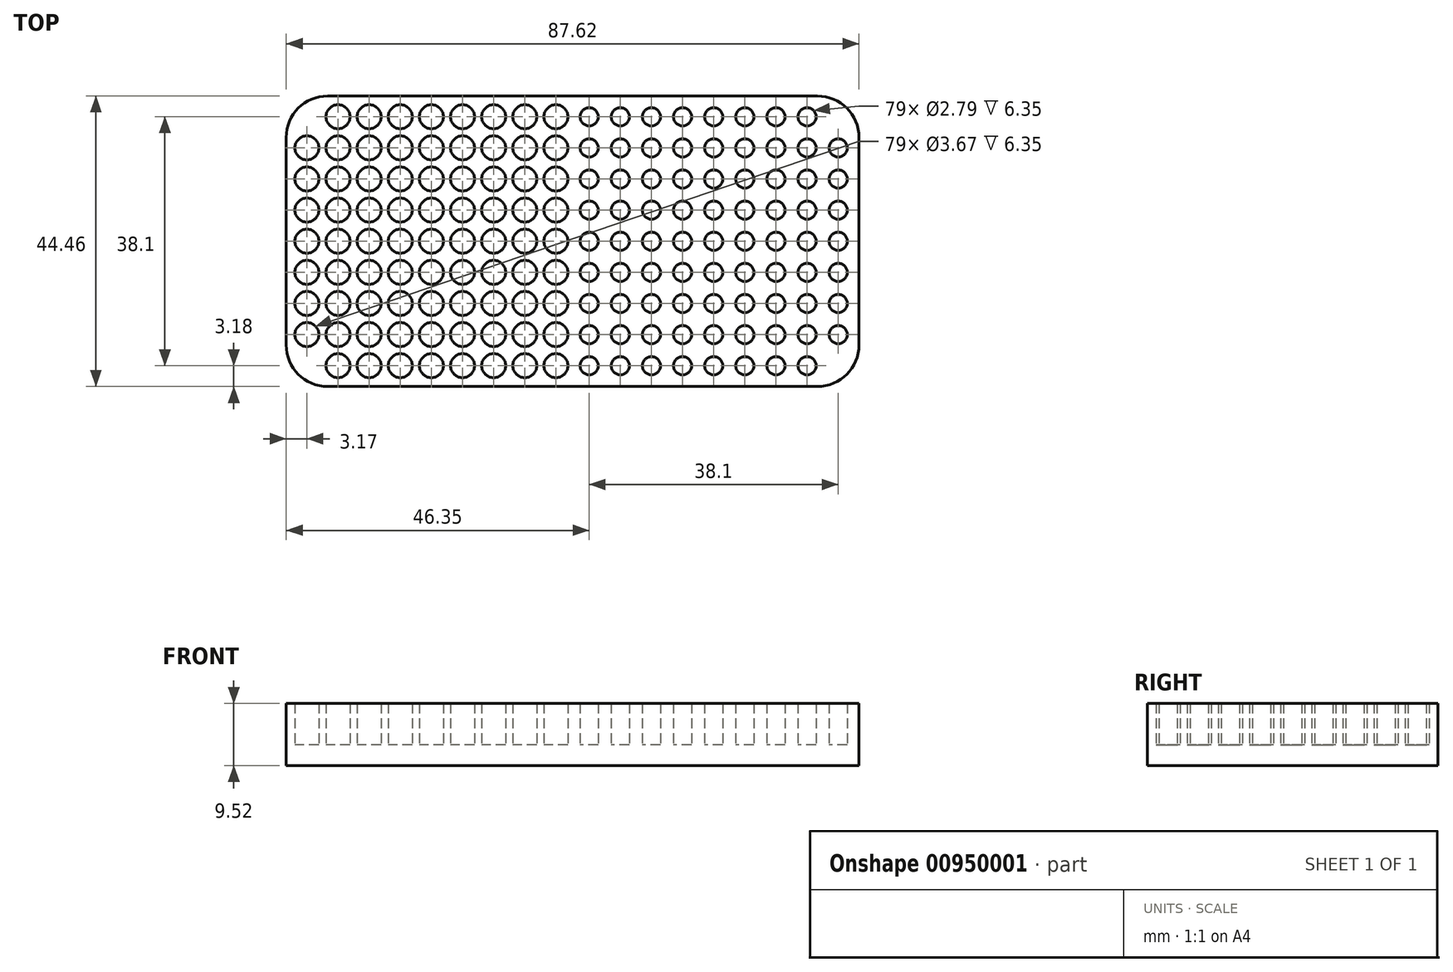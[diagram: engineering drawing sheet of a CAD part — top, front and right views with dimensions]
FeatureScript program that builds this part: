
annotation { "Feature Type Name" : "Feature", "Feature Type Description" : "" }
export const myFeature = defineFeature(function(context is Context, id is Id, definition is map)
    precondition{}
    {
        {
            var Q0;
            Q0=qCreatedBy(makeId("Top.planeOp"),FACE);
            var sketch = newSketch(context, id + "F0", { "sketchPlane" : qUnion([Q0])});
            skLineSegment(sketch, "E0.bottom", {"start": v(43.82, 22.23) * mm, "end": v(-43.82, 22.23) * mm});
            skLineSegment(sketch, "E0.top", {"start": v(43.82, -22.23) * mm, "end": v(-43.82, -22.23) * mm});
            skLineSegment(sketch, "E0.left", {"start": v(43.82, 22.23) * mm, "end": v(43.82, -22.23) * mm});
            skLineSegment(sketch, "E0.right", {"start": v(-43.82, 22.23) * mm, "end": v(-43.82, -22.23) * mm});
            skPoint(sketch, "E0.middle", {"position": v(0, 0) * mm});
            skCircle(sketch, "E1", {"center": v(-40.64, 19.05) * mm, "radius": 1.84 * mm, "construction": true});
            skCircle(sketch, "E2", {"center": v(40.64, 19.05) * mm, "radius": 1.4 * mm, "construction": true});
            skCircle(sketch, "E3.0.1.0", {"center": v(-40.64, 14.29) * mm, "radius": 1.84 * mm});
            skCircle(sketch, "E3.0.2.0", {"center": v(-40.64, 9.53) * mm, "radius": 1.84 * mm});
            skCircle(sketch, "E3.0.3.0", {"center": v(-40.64, 4.76) * mm, "radius": 1.84 * mm});
            skCircle(sketch, "E3.0.4.0", {"center": v(-40.64, 0) * mm, "radius": 1.84 * mm});
            skCircle(sketch, "E3.0.5.0", {"center": v(-40.64, -4.76) * mm, "radius": 1.84 * mm});
            skCircle(sketch, "E3.0.6.0", {"center": v(-40.64, -9.52) * mm, "radius": 1.84 * mm});
            skCircle(sketch, "E3.0.7.0", {"center": v(-40.64, -14.29) * mm, "radius": 1.84 * mm});
            skCircle(sketch, "E3.1.0.0", {"center": v(-35.88, 19.05) * mm, "radius": 1.84 * mm});
            skCircle(sketch, "E3.1.1.0", {"center": v(-35.88, 14.29) * mm, "radius": 1.84 * mm});
            skCircle(sketch, "E3.1.2.0", {"center": v(-35.88, 9.53) * mm, "radius": 1.84 * mm});
            skCircle(sketch, "E3.1.3.0", {"center": v(-35.88, 4.76) * mm, "radius": 1.84 * mm});
            skCircle(sketch, "E3.1.4.0", {"center": v(-35.88, 0) * mm, "radius": 1.84 * mm});
            skCircle(sketch, "E3.1.5.0", {"center": v(-35.88, -4.76) * mm, "radius": 1.84 * mm});
            skCircle(sketch, "E3.1.6.0", {"center": v(-35.88, -9.52) * mm, "radius": 1.84 * mm});
            skCircle(sketch, "E3.1.7.0", {"center": v(-35.88, -14.29) * mm, "radius": 1.84 * mm});
            skCircle(sketch, "E3.2.0.0", {"center": v(-31.12, 19.05) * mm, "radius": 1.84 * mm});
            skCircle(sketch, "E3.2.1.0", {"center": v(-31.12, 14.29) * mm, "radius": 1.84 * mm});
            skCircle(sketch, "E3.2.2.0", {"center": v(-31.12, 9.53) * mm, "radius": 1.84 * mm});
            skCircle(sketch, "E3.2.3.0", {"center": v(-31.12, 4.76) * mm, "radius": 1.84 * mm});
            skCircle(sketch, "E3.2.4.0", {"center": v(-31.12, 0) * mm, "radius": 1.84 * mm});
            skCircle(sketch, "E3.2.5.0", {"center": v(-31.12, -4.76) * mm, "radius": 1.84 * mm});
            skCircle(sketch, "E3.2.6.0", {"center": v(-31.12, -9.52) * mm, "radius": 1.84 * mm});
            skCircle(sketch, "E3.2.7.0", {"center": v(-31.12, -14.29) * mm, "radius": 1.84 * mm});
            skCircle(sketch, "E3.3.0.0", {"center": v(-26.35, 19.05) * mm, "radius": 1.84 * mm});
            skCircle(sketch, "E3.3.1.0", {"center": v(-26.35, 14.29) * mm, "radius": 1.84 * mm});
            skCircle(sketch, "E3.3.2.0", {"center": v(-26.35, 9.53) * mm, "radius": 1.84 * mm});
            skCircle(sketch, "E3.3.3.0", {"center": v(-26.35, 4.76) * mm, "radius": 1.84 * mm});
            skCircle(sketch, "E3.3.4.0", {"center": v(-26.35, 0) * mm, "radius": 1.84 * mm});
            skCircle(sketch, "E3.3.5.0", {"center": v(-26.35, -4.76) * mm, "radius": 1.84 * mm});
            skCircle(sketch, "E3.3.6.0", {"center": v(-26.35, -9.52) * mm, "radius": 1.84 * mm});
            skCircle(sketch, "E3.3.7.0", {"center": v(-26.35, -14.29) * mm, "radius": 1.84 * mm});
            skCircle(sketch, "E3.4.0.0", {"center": v(-21.59, 19.05) * mm, "radius": 1.84 * mm});
            skCircle(sketch, "E3.4.1.0", {"center": v(-21.59, 14.29) * mm, "radius": 1.84 * mm});
            skCircle(sketch, "E3.4.2.0", {"center": v(-21.59, 9.53) * mm, "radius": 1.84 * mm});
            skCircle(sketch, "E3.4.3.0", {"center": v(-21.59, 4.76) * mm, "radius": 1.84 * mm});
            skCircle(sketch, "E3.4.4.0", {"center": v(-21.59, 0) * mm, "radius": 1.84 * mm});
            skCircle(sketch, "E3.4.5.0", {"center": v(-21.59, -4.76) * mm, "radius": 1.84 * mm});
            skCircle(sketch, "E3.4.6.0", {"center": v(-21.59, -9.52) * mm, "radius": 1.84 * mm});
            skCircle(sketch, "E3.4.7.0", {"center": v(-21.59, -14.29) * mm, "radius": 1.84 * mm});
            skCircle(sketch, "E3.5.0.0", {"center": v(-16.83, 19.05) * mm, "radius": 1.84 * mm});
            skCircle(sketch, "E3.5.1.0", {"center": v(-16.83, 14.29) * mm, "radius": 1.84 * mm});
            skCircle(sketch, "E3.5.2.0", {"center": v(-16.83, 9.53) * mm, "radius": 1.84 * mm});
            skCircle(sketch, "E3.5.3.0", {"center": v(-16.83, 4.76) * mm, "radius": 1.84 * mm});
            skCircle(sketch, "E3.5.4.0", {"center": v(-16.83, 0) * mm, "radius": 1.84 * mm});
            skCircle(sketch, "E3.5.5.0", {"center": v(-16.83, -4.76) * mm, "radius": 1.84 * mm});
            skCircle(sketch, "E3.5.6.0", {"center": v(-16.83, -9.52) * mm, "radius": 1.84 * mm});
            skCircle(sketch, "E3.5.7.0", {"center": v(-16.83, -14.29) * mm, "radius": 1.84 * mm});
            skCircle(sketch, "E3.6.0.0", {"center": v(-12.06, 19.05) * mm, "radius": 1.84 * mm});
            skCircle(sketch, "E3.6.1.0", {"center": v(-12.06, 14.29) * mm, "radius": 1.84 * mm});
            skCircle(sketch, "E3.6.2.0", {"center": v(-12.06, 9.53) * mm, "radius": 1.84 * mm});
            skCircle(sketch, "E3.6.3.0", {"center": v(-12.06, 4.76) * mm, "radius": 1.84 * mm});
            skCircle(sketch, "E3.6.4.0", {"center": v(-12.06, 0) * mm, "radius": 1.84 * mm});
            skCircle(sketch, "E3.6.5.0", {"center": v(-12.06, -4.76) * mm, "radius": 1.84 * mm});
            skCircle(sketch, "E3.6.6.0", {"center": v(-12.06, -9.52) * mm, "radius": 1.84 * mm});
            skCircle(sketch, "E3.6.7.0", {"center": v(-12.06, -14.29) * mm, "radius": 1.84 * mm});
            skCircle(sketch, "E3.7.0.0", {"center": v(-7.3, 19.05) * mm, "radius": 1.84 * mm});
            skCircle(sketch, "E3.7.1.0", {"center": v(-7.3, 14.29) * mm, "radius": 1.84 * mm});
            skCircle(sketch, "E3.7.2.0", {"center": v(-7.3, 9.53) * mm, "radius": 1.84 * mm});
            skCircle(sketch, "E3.7.3.0", {"center": v(-7.3, 4.76) * mm, "radius": 1.84 * mm});
            skCircle(sketch, "E3.7.4.0", {"center": v(-7.3, 0) * mm, "radius": 1.84 * mm});
            skCircle(sketch, "E3.7.5.0", {"center": v(-7.3, -4.76) * mm, "radius": 1.84 * mm});
            skCircle(sketch, "E3.7.6.0", {"center": v(-7.3, -9.52) * mm, "radius": 1.84 * mm});
            skCircle(sketch, "E3.7.7.0", {"center": v(-7.3, -14.29) * mm, "radius": 1.84 * mm});
            skCircle(sketch, "E3.8.0.0", {"center": v(-2.54, 19.05) * mm, "radius": 1.84 * mm});
            skCircle(sketch, "E3.8.1.0", {"center": v(-2.54, 14.29) * mm, "radius": 1.84 * mm});
            skCircle(sketch, "E3.8.2.0", {"center": v(-2.54, 9.53) * mm, "radius": 1.84 * mm});
            skCircle(sketch, "E3.8.3.0", {"center": v(-2.54, 4.76) * mm, "radius": 1.84 * mm});
            skCircle(sketch, "E3.8.4.0", {"center": v(-2.54, 0) * mm, "radius": 1.84 * mm});
            skCircle(sketch, "E3.8.5.0", {"center": v(-2.54, -4.76) * mm, "radius": 1.84 * mm});
            skCircle(sketch, "E3.8.6.0", {"center": v(-2.54, -9.52) * mm, "radius": 1.84 * mm});
            skCircle(sketch, "E3.8.7.0", {"center": v(-2.54, -14.29) * mm, "radius": 1.84 * mm});
            skLineSegment(sketch, "E3.direction1", {"start": v(-40.64, 19.05) * mm, "end": v(-35.88, 19.05) * mm, "construction": true});
            skLineSegment(sketch, "E3.direction2", {"start": v(-40.64, 19.05) * mm, "end": v(-40.64, 14.29) * mm, "construction": true});
            skCircle(sketch, "E4.0.0.8", {"center": v(-40.64, -19.05) * mm, "radius": 1.84 * mm, "construction": true});
            skCircle(sketch, "E4.0.1.8", {"center": v(-35.88, -19.05) * mm, "radius": 1.84 * mm});
            skCircle(sketch, "E4.0.2.8", {"center": v(-31.11, -19.05) * mm, "radius": 1.84 * mm});
            skCircle(sketch, "E4.0.3.8", {"center": v(-26.35, -19.05) * mm, "radius": 1.84 * mm});
            skCircle(sketch, "E4.0.4.8", {"center": v(-21.59, -19.05) * mm, "radius": 1.84 * mm});
            skCircle(sketch, "E4.0.5.8", {"center": v(-16.83, -19.05) * mm, "radius": 1.84 * mm});
            skCircle(sketch, "E4.0.6.8", {"center": v(-12.06, -19.05) * mm, "radius": 1.84 * mm});
            skCircle(sketch, "E4.0.7.8", {"center": v(-7.3, -19.05) * mm, "radius": 1.84 * mm});
            skCircle(sketch, "E4.0.8.8", {"center": v(-2.54, -19.05) * mm, "radius": 1.84 * mm});
            skCircle(sketch, "E5.0.1.0", {"center": v(40.64, 14.29) * mm, "radius": 1.4 * mm});
            skCircle(sketch, "E5.0.2.0", {"center": v(40.64, 9.53) * mm, "radius": 1.4 * mm});
            skCircle(sketch, "E5.0.3.0", {"center": v(40.64, 4.76) * mm, "radius": 1.4 * mm});
            skCircle(sketch, "E5.0.4.0", {"center": v(40.64, 0) * mm, "radius": 1.4 * mm});
            skCircle(sketch, "E5.0.5.0", {"center": v(40.64, -4.76) * mm, "radius": 1.4 * mm});
            skCircle(sketch, "E5.0.6.0", {"center": v(40.64, -9.52) * mm, "radius": 1.4 * mm});
            skCircle(sketch, "E5.0.7.0", {"center": v(40.64, -14.29) * mm, "radius": 1.4 * mm});
            skCircle(sketch, "E5.0.8.0", {"center": v(40.64, -19.05) * mm, "radius": 1.4 * mm, "construction": true});
            skCircle(sketch, "E5.1.0.0", {"center": v(35.88, 19.05) * mm, "radius": 1.4 * mm});
            skCircle(sketch, "E5.1.1.0", {"center": v(35.88, 14.29) * mm, "radius": 1.4 * mm});
            skCircle(sketch, "E5.1.2.0", {"center": v(35.88, 9.53) * mm, "radius": 1.4 * mm});
            skCircle(sketch, "E5.1.3.0", {"center": v(35.88, 4.76) * mm, "radius": 1.4 * mm});
            skCircle(sketch, "E5.1.4.0", {"center": v(35.88, 0) * mm, "radius": 1.4 * mm});
            skCircle(sketch, "E5.1.5.0", {"center": v(35.88, -4.76) * mm, "radius": 1.4 * mm});
            skCircle(sketch, "E5.1.6.0", {"center": v(35.88, -9.52) * mm, "radius": 1.4 * mm});
            skCircle(sketch, "E5.1.7.0", {"center": v(35.88, -14.29) * mm, "radius": 1.4 * mm});
            skCircle(sketch, "E5.1.8.0", {"center": v(35.88, -19.05) * mm, "radius": 1.4 * mm});
            skCircle(sketch, "E5.2.0.0", {"center": v(31.12, 19.05) * mm, "radius": 1.4 * mm});
            skCircle(sketch, "E5.2.1.0", {"center": v(31.12, 14.29) * mm, "radius": 1.4 * mm});
            skCircle(sketch, "E5.2.2.0", {"center": v(31.12, 9.53) * mm, "radius": 1.4 * mm});
            skCircle(sketch, "E5.2.3.0", {"center": v(31.12, 4.76) * mm, "radius": 1.4 * mm});
            skCircle(sketch, "E5.2.4.0", {"center": v(31.12, 0) * mm, "radius": 1.4 * mm});
            skCircle(sketch, "E5.2.5.0", {"center": v(31.12, -4.76) * mm, "radius": 1.4 * mm});
            skCircle(sketch, "E5.2.6.0", {"center": v(31.12, -9.52) * mm, "radius": 1.4 * mm});
            skCircle(sketch, "E5.2.7.0", {"center": v(31.12, -14.29) * mm, "radius": 1.4 * mm});
            skCircle(sketch, "E5.2.8.0", {"center": v(31.12, -19.05) * mm, "radius": 1.4 * mm});
            skCircle(sketch, "E5.3.0.0", {"center": v(26.35, 19.05) * mm, "radius": 1.4 * mm});
            skCircle(sketch, "E5.3.1.0", {"center": v(26.35, 14.29) * mm, "radius": 1.4 * mm});
            skCircle(sketch, "E5.3.2.0", {"center": v(26.35, 9.53) * mm, "radius": 1.4 * mm});
            skCircle(sketch, "E5.3.3.0", {"center": v(26.35, 4.76) * mm, "radius": 1.4 * mm});
            skCircle(sketch, "E5.3.4.0", {"center": v(26.35, 0) * mm, "radius": 1.4 * mm});
            skCircle(sketch, "E5.3.5.0", {"center": v(26.35, -4.76) * mm, "radius": 1.4 * mm});
            skCircle(sketch, "E5.3.6.0", {"center": v(26.35, -9.52) * mm, "radius": 1.4 * mm});
            skCircle(sketch, "E5.3.7.0", {"center": v(26.35, -14.29) * mm, "radius": 1.4 * mm});
            skCircle(sketch, "E5.3.8.0", {"center": v(26.35, -19.05) * mm, "radius": 1.4 * mm});
            skCircle(sketch, "E5.4.0.0", {"center": v(21.6, 19.05) * mm, "radius": 1.4 * mm});
            skCircle(sketch, "E5.4.1.0", {"center": v(21.6, 14.29) * mm, "radius": 1.4 * mm});
            skCircle(sketch, "E5.4.2.0", {"center": v(21.6, 9.53) * mm, "radius": 1.4 * mm});
            skCircle(sketch, "E5.4.3.0", {"center": v(21.6, 4.76) * mm, "radius": 1.4 * mm});
            skCircle(sketch, "E5.4.4.0", {"center": v(21.6, 0) * mm, "radius": 1.4 * mm});
            skCircle(sketch, "E5.4.5.0", {"center": v(21.6, -4.76) * mm, "radius": 1.4 * mm});
            skCircle(sketch, "E5.4.6.0", {"center": v(21.6, -9.52) * mm, "radius": 1.4 * mm});
            skCircle(sketch, "E5.4.7.0", {"center": v(21.6, -14.29) * mm, "radius": 1.4 * mm});
            skCircle(sketch, "E5.4.8.0", {"center": v(21.6, -19.05) * mm, "radius": 1.4 * mm});
            skCircle(sketch, "E5.5.0.0", {"center": v(16.83, 19.05) * mm, "radius": 1.4 * mm});
            skCircle(sketch, "E5.5.1.0", {"center": v(16.83, 14.29) * mm, "radius": 1.4 * mm});
            skCircle(sketch, "E5.5.2.0", {"center": v(16.83, 9.53) * mm, "radius": 1.4 * mm});
            skCircle(sketch, "E5.5.3.0", {"center": v(16.83, 4.76) * mm, "radius": 1.4 * mm});
            skCircle(sketch, "E5.5.4.0", {"center": v(16.83, 0) * mm, "radius": 1.4 * mm});
            skCircle(sketch, "E5.5.5.0", {"center": v(16.83, -4.76) * mm, "radius": 1.4 * mm});
            skCircle(sketch, "E5.5.6.0", {"center": v(16.83, -9.52) * mm, "radius": 1.4 * mm});
            skCircle(sketch, "E5.5.7.0", {"center": v(16.83, -14.29) * mm, "radius": 1.4 * mm});
            skCircle(sketch, "E5.5.8.0", {"center": v(16.83, -19.05) * mm, "radius": 1.4 * mm});
            skCircle(sketch, "E5.6.0.0", {"center": v(12.07, 19.05) * mm, "radius": 1.4 * mm});
            skCircle(sketch, "E5.6.1.0", {"center": v(12.07, 14.29) * mm, "radius": 1.4 * mm});
            skCircle(sketch, "E5.6.2.0", {"center": v(12.07, 9.53) * mm, "radius": 1.4 * mm});
            skCircle(sketch, "E5.6.3.0", {"center": v(12.07, 4.76) * mm, "radius": 1.4 * mm});
            skCircle(sketch, "E5.6.4.0", {"center": v(12.07, 0) * mm, "radius": 1.4 * mm});
            skCircle(sketch, "E5.6.5.0", {"center": v(12.07, -4.76) * mm, "radius": 1.4 * mm});
            skCircle(sketch, "E5.6.6.0", {"center": v(12.07, -9.52) * mm, "radius": 1.4 * mm});
            skCircle(sketch, "E5.6.7.0", {"center": v(12.07, -14.29) * mm, "radius": 1.4 * mm});
            skCircle(sketch, "E5.6.8.0", {"center": v(12.07, -19.05) * mm, "radius": 1.4 * mm});
            skCircle(sketch, "E5.7.0.0", {"center": v(7.3, 19.05) * mm, "radius": 1.4 * mm});
            skCircle(sketch, "E5.7.1.0", {"center": v(7.3, 14.29) * mm, "radius": 1.4 * mm});
            skCircle(sketch, "E5.7.2.0", {"center": v(7.3, 9.53) * mm, "radius": 1.4 * mm});
            skCircle(sketch, "E5.7.3.0", {"center": v(7.3, 4.76) * mm, "radius": 1.4 * mm});
            skCircle(sketch, "E5.7.4.0", {"center": v(7.3, 0) * mm, "radius": 1.4 * mm});
            skCircle(sketch, "E5.7.5.0", {"center": v(7.3, -4.76) * mm, "radius": 1.4 * mm});
            skCircle(sketch, "E5.7.6.0", {"center": v(7.3, -9.52) * mm, "radius": 1.4 * mm});
            skCircle(sketch, "E5.7.7.0", {"center": v(7.3, -14.29) * mm, "radius": 1.4 * mm});
            skCircle(sketch, "E5.7.8.0", {"center": v(7.3, -19.05) * mm, "radius": 1.4 * mm});
            skCircle(sketch, "E5.8.0.0", {"center": v(2.54, 19.05) * mm, "radius": 1.4 * mm});
            skCircle(sketch, "E5.8.1.0", {"center": v(2.54, 14.29) * mm, "radius": 1.4 * mm});
            skCircle(sketch, "E5.8.2.0", {"center": v(2.54, 9.53) * mm, "radius": 1.4 * mm});
            skCircle(sketch, "E5.8.3.0", {"center": v(2.54, 4.76) * mm, "radius": 1.4 * mm});
            skCircle(sketch, "E5.8.4.0", {"center": v(2.54, 0) * mm, "radius": 1.4 * mm});
            skCircle(sketch, "E5.8.5.0", {"center": v(2.54, -4.76) * mm, "radius": 1.4 * mm});
            skCircle(sketch, "E5.8.6.0", {"center": v(2.54, -9.52) * mm, "radius": 1.4 * mm});
            skCircle(sketch, "E5.8.7.0", {"center": v(2.54, -14.29) * mm, "radius": 1.4 * mm});
            skCircle(sketch, "E5.8.8.0", {"center": v(2.54, -19.05) * mm, "radius": 1.4 * mm});
            skLineSegment(sketch, "E5.direction1", {"start": v(40.64, 19.05) * mm, "end": v(35.88, 19.05) * mm, "construction": true});
            skLineSegment(sketch, "E5.direction2", {"start": v(40.64, 19.05) * mm, "end": v(40.64, 14.29) * mm, "construction": true});
            skSolve(sketch);
        }
        {
            var Q0;
            Q0=makeQuery(id+"F0.imprint","IMPRINT",FACE,{"disambiguationData":[TD([[makeQuery(id+"F0.imprint","IMPRINT",EDGE,{"derivedFrom":sQuery(id+"F0.wireOp",EDGE,"E0.bottom")}),1.0]])]});
            var Q1;
            Q1=makeQuery(id+"F0.imprint","IMPRINT",FACE,{"disambiguationData":[TD([[makeQuery(id+"F0.imprint","IMPRINT",EDGE,{"derivedFrom":sQuery(id+"F0.wireOp",EDGE,"E5.6.1.0")}),1.0]])]});
            var Q2;
            Q2=makeQuery(id+"F0.imprint","IMPRINT",FACE,{"disambiguationData":[TD([[makeQuery(id+"F0.imprint","IMPRINT",EDGE,{"derivedFrom":sQuery(id+"F0.wireOp",EDGE,"E4.0.5.8")}),1.0]])]});
            var Q3;
            Q3=makeQuery(id+"F0.imprint","IMPRINT",FACE,{"disambiguationData":[TD([[makeQuery(id+"F0.imprint","IMPRINT",EDGE,{"derivedFrom":sQuery(id+"F0.wireOp",EDGE,"E5.5.0.0")}),1.0]])]});
            var Q4;
            Q4=makeQuery(id+"F0.imprint","IMPRINT",FACE,{"disambiguationData":[TD([[makeQuery(id+"F0.imprint","IMPRINT",EDGE,{"derivedFrom":sQuery(id+"F0.wireOp",EDGE,"E3.5.3.0")}),1.0]])]});
            var Q5;
            Q5=makeQuery(id+"F0.imprint","IMPRINT",FACE,{"disambiguationData":[TD([[makeQuery(id+"F0.imprint","IMPRINT",EDGE,{"derivedFrom":sQuery(id+"F0.wireOp",EDGE,"E3.1.4.0")}),1.0]])]});
            var Q6;
            Q6=makeQuery(id+"F0.imprint","IMPRINT",FACE,{"disambiguationData":[TD([[makeQuery(id+"F0.imprint","IMPRINT",EDGE,{"derivedFrom":sQuery(id+"F0.wireOp",EDGE,"E3.7.0.0")}),1.0]])]});
            var Q7;
            Q7=makeQuery(id+"F0.imprint","IMPRINT",FACE,{"disambiguationData":[TD([[makeQuery(id+"F0.imprint","IMPRINT",EDGE,{"derivedFrom":sQuery(id+"F0.wireOp",EDGE,"E5.0.7.0")}),1.0]])]});
            var Q8;
            Q8=makeQuery(id+"F0.imprint","IMPRINT",FACE,{"disambiguationData":[TD([[makeQuery(id+"F0.imprint","IMPRINT",EDGE,{"derivedFrom":sQuery(id+"F0.wireOp",EDGE,"E5.0.5.0")}),1.0]])]});
            var Q9;
            Q9=makeQuery(id+"F0.imprint","IMPRINT",FACE,{"disambiguationData":[TD([[makeQuery(id+"F0.imprint","IMPRINT",EDGE,{"derivedFrom":sQuery(id+"F0.wireOp",EDGE,"E5.2.4.0")}),1.0]])]});
            var Q10;
            Q10=makeQuery(id+"F0.imprint","IMPRINT",FACE,{"disambiguationData":[TD([[makeQuery(id+"F0.imprint","IMPRINT",EDGE,{"derivedFrom":sQuery(id+"F0.wireOp",EDGE,"E5.3.3.0")}),1.0]])]});
            var Q11;
            Q11=makeQuery(id+"F0.imprint","IMPRINT",FACE,{"disambiguationData":[TD([[makeQuery(id+"F0.imprint","IMPRINT",EDGE,{"derivedFrom":sQuery(id+"F0.wireOp",EDGE,"E5.8.6.0")}),1.0]])]});
            var Q12;
            Q12=makeQuery(id+"F0.imprint","IMPRINT",FACE,{"disambiguationData":[TD([[makeQuery(id+"F0.imprint","IMPRINT",EDGE,{"derivedFrom":sQuery(id+"F0.wireOp",EDGE,"E3.4.0.0")}),1.0]])]});
            var Q13;
            Q13=makeQuery(id+"F0.imprint","IMPRINT",FACE,{"disambiguationData":[TD([[makeQuery(id+"F0.imprint","IMPRINT",EDGE,{"derivedFrom":sQuery(id+"F0.wireOp",EDGE,"E3.8.4.0")}),1.0]])]});
            var Q14;
            Q14=makeQuery(id+"F0.imprint","IMPRINT",FACE,{"disambiguationData":[TD([[makeQuery(id+"F0.imprint","IMPRINT",EDGE,{"derivedFrom":sQuery(id+"F0.wireOp",EDGE,"E3.6.0.0")}),1.0]])]});
            var Q15;
            Q15=makeQuery(id+"F0.imprint","IMPRINT",FACE,{"disambiguationData":[TD([[makeQuery(id+"F0.imprint","IMPRINT",EDGE,{"derivedFrom":sQuery(id+"F0.wireOp",EDGE,"E3.6.6.0")}),1.0]])]});
            var Q16;
            Q16=makeQuery(id+"F0.imprint","IMPRINT",FACE,{"disambiguationData":[TD([[makeQuery(id+"F0.imprint","IMPRINT",EDGE,{"derivedFrom":sQuery(id+"F0.wireOp",EDGE,"E3.4.7.0")}),1.0]])]});
            var Q17;
            Q17=makeQuery(id+"F0.imprint","IMPRINT",FACE,{"disambiguationData":[TD([[makeQuery(id+"F0.imprint","IMPRINT",EDGE,{"derivedFrom":sQuery(id+"F0.wireOp",EDGE,"E3.3.0.0")}),1.0]])]});
            var Q18;
            Q18=makeQuery(id+"F0.imprint","IMPRINT",FACE,{"disambiguationData":[TD([[makeQuery(id+"F0.imprint","IMPRINT",EDGE,{"derivedFrom":sQuery(id+"F0.wireOp",EDGE,"E3.7.2.0")}),1.0]])]});
            var Q19;
            Q19=makeQuery(id+"F0.imprint","IMPRINT",FACE,{"disambiguationData":[TD([[makeQuery(id+"F0.imprint","IMPRINT",EDGE,{"derivedFrom":sQuery(id+"F0.wireOp",EDGE,"E5.4.3.0")}),1.0]])]});
            var Q20;
            Q20=makeQuery(id+"F0.imprint","IMPRINT",FACE,{"disambiguationData":[TD([[makeQuery(id+"F0.imprint","IMPRINT",EDGE,{"derivedFrom":sQuery(id+"F0.wireOp",EDGE,"E3.3.1.0")}),1.0]])]});
            var Q21;
            Q21=makeQuery(id+"F0.imprint","IMPRINT",FACE,{"disambiguationData":[TD([[makeQuery(id+"F0.imprint","IMPRINT",EDGE,{"derivedFrom":sQuery(id+"F0.wireOp",EDGE,"E3.1.2.0")}),1.0]])]});
            var Q22;
            Q22=makeQuery(id+"F0.imprint","IMPRINT",FACE,{"disambiguationData":[TD([[makeQuery(id+"F0.imprint","IMPRINT",EDGE,{"derivedFrom":sQuery(id+"F0.wireOp",EDGE,"E5.6.0.0")}),1.0]])]});
            var Q23;
            Q23=makeQuery(id+"F0.imprint","IMPRINT",FACE,{"disambiguationData":[TD([[makeQuery(id+"F0.imprint","IMPRINT",EDGE,{"derivedFrom":sQuery(id+"F0.wireOp",EDGE,"E3.4.6.0")}),1.0]])]});
            var Q24;
            Q24=makeQuery(id+"F0.imprint","IMPRINT",FACE,{"disambiguationData":[TD([[makeQuery(id+"F0.imprint","IMPRINT",EDGE,{"derivedFrom":sQuery(id+"F0.wireOp",EDGE,"E5.2.3.0")}),1.0]])]});
            var Q25;
            Q25=makeQuery(id+"F0.imprint","IMPRINT",FACE,{"disambiguationData":[TD([[makeQuery(id+"F0.imprint","IMPRINT",EDGE,{"derivedFrom":sQuery(id+"F0.wireOp",EDGE,"E4.0.1.8")}),1.0]])]});
            var Q26;
            Q26=makeQuery(id+"F0.imprint","IMPRINT",FACE,{"disambiguationData":[TD([[makeQuery(id+"F0.imprint","IMPRINT",EDGE,{"derivedFrom":sQuery(id+"F0.wireOp",EDGE,"E5.6.5.0")}),1.0]])]});
            var Q27;
            Q27=makeQuery(id+"F0.imprint","IMPRINT",FACE,{"disambiguationData":[TD([[makeQuery(id+"F0.imprint","IMPRINT",EDGE,{"derivedFrom":sQuery(id+"F0.wireOp",EDGE,"E3.8.6.0")}),1.0]])]});
            var Q28;
            Q28=makeQuery(id+"F0.imprint","IMPRINT",FACE,{"disambiguationData":[TD([[makeQuery(id+"F0.imprint","IMPRINT",EDGE,{"derivedFrom":sQuery(id+"F0.wireOp",EDGE,"E5.0.6.0")}),1.0]])]});
            var Q29;
            Q29=makeQuery(id+"F0.imprint","IMPRINT",FACE,{"disambiguationData":[TD([[makeQuery(id+"F0.imprint","IMPRINT",EDGE,{"derivedFrom":sQuery(id+"F0.wireOp",EDGE,"E3.1.5.0")}),1.0]])]});
            var Q30;
            Q30=makeQuery(id+"F0.imprint","IMPRINT",FACE,{"disambiguationData":[TD([[makeQuery(id+"F0.imprint","IMPRINT",EDGE,{"derivedFrom":sQuery(id+"F0.wireOp",EDGE,"E3.8.5.0")}),1.0]])]});
            var Q31;
            Q31=makeQuery(id+"F0.imprint","IMPRINT",FACE,{"disambiguationData":[TD([[makeQuery(id+"F0.imprint","IMPRINT",EDGE,{"derivedFrom":sQuery(id+"F0.wireOp",EDGE,"E3.4.2.0")}),1.0]])]});
            var Q32;
            Q32=makeQuery(id+"F0.imprint","IMPRINT",FACE,{"disambiguationData":[TD([[makeQuery(id+"F0.imprint","IMPRINT",EDGE,{"derivedFrom":sQuery(id+"F0.wireOp",EDGE,"E3.4.4.0")}),1.0]])]});
            var Q33;
            Q33=makeQuery(id+"F0.imprint","IMPRINT",FACE,{"disambiguationData":[TD([[makeQuery(id+"F0.imprint","IMPRINT",EDGE,{"derivedFrom":sQuery(id+"F0.wireOp",EDGE,"E3.4.5.0")}),1.0]])]});
            var Q34;
            Q34=makeQuery(id+"F0.imprint","IMPRINT",FACE,{"disambiguationData":[TD([[makeQuery(id+"F0.imprint","IMPRINT",EDGE,{"derivedFrom":sQuery(id+"F0.wireOp",EDGE,"E5.7.8.0")}),1.0]])]});
            var Q35;
            Q35=makeQuery(id+"F0.imprint","IMPRINT",FACE,{"disambiguationData":[TD([[makeQuery(id+"F0.imprint","IMPRINT",EDGE,{"derivedFrom":sQuery(id+"F0.wireOp",EDGE,"E3.3.5.0")}),1.0]])]});
            var Q36;
            Q36=makeQuery(id+"F0.imprint","IMPRINT",FACE,{"disambiguationData":[TD([[makeQuery(id+"F0.imprint","IMPRINT",EDGE,{"derivedFrom":sQuery(id+"F0.wireOp",EDGE,"E5.5.2.0")}),1.0]])]});
            var Q37;
            Q37=makeQuery(id+"F0.imprint","IMPRINT",FACE,{"disambiguationData":[TD([[makeQuery(id+"F0.imprint","IMPRINT",EDGE,{"derivedFrom":sQuery(id+"F0.wireOp",EDGE,"E3.7.1.0")}),1.0]])]});
            var Q38;
            Q38=makeQuery(id+"F0.imprint","IMPRINT",FACE,{"disambiguationData":[TD([[makeQuery(id+"F0.imprint","IMPRINT",EDGE,{"derivedFrom":sQuery(id+"F0.wireOp",EDGE,"E3.1.1.0")}),1.0]])]});
            var Q39;
            Q39=makeQuery(id+"F0.imprint","IMPRINT",FACE,{"disambiguationData":[TD([[makeQuery(id+"F0.imprint","IMPRINT",EDGE,{"derivedFrom":sQuery(id+"F0.wireOp",EDGE,"E3.1.0.0")}),1.0]])]});
            var Q40;
            Q40=makeQuery(id+"F0.imprint","IMPRINT",FACE,{"disambiguationData":[TD([[makeQuery(id+"F0.imprint","IMPRINT",EDGE,{"derivedFrom":sQuery(id+"F0.wireOp",EDGE,"E3.2.6.0")}),1.0]])]});
            var Q41;
            Q41=makeQuery(id+"F0.imprint","IMPRINT",FACE,{"disambiguationData":[TD([[makeQuery(id+"F0.imprint","IMPRINT",EDGE,{"derivedFrom":sQuery(id+"F0.wireOp",EDGE,"E5.5.1.0")}),1.0]])]});
            var Q42;
            Q42=makeQuery(id+"F0.imprint","IMPRINT",FACE,{"disambiguationData":[TD([[makeQuery(id+"F0.imprint","IMPRINT",EDGE,{"derivedFrom":sQuery(id+"F0.wireOp",EDGE,"E3.2.3.0")}),1.0]])]});
            var Q43;
            Q43=makeQuery(id+"F0.imprint","IMPRINT",FACE,{"disambiguationData":[TD([[makeQuery(id+"F0.imprint","IMPRINT",EDGE,{"derivedFrom":sQuery(id+"F0.wireOp",EDGE,"E3.3.2.0")}),1.0]])]});
            var Q44;
            Q44=makeQuery(id+"F0.imprint","IMPRINT",FACE,{"disambiguationData":[TD([[makeQuery(id+"F0.imprint","IMPRINT",EDGE,{"derivedFrom":sQuery(id+"F0.wireOp",EDGE,"E3.5.7.0")}),1.0]])]});
            var Q45;
            Q45=makeQuery(id+"F0.imprint","IMPRINT",FACE,{"disambiguationData":[TD([[makeQuery(id+"F0.imprint","IMPRINT",EDGE,{"derivedFrom":sQuery(id+"F0.wireOp",EDGE,"E4.0.7.8")}),1.0]])]});
            var Q46;
            Q46=makeQuery(id+"F0.imprint","IMPRINT",FACE,{"disambiguationData":[TD([[makeQuery(id+"F0.imprint","IMPRINT",EDGE,{"derivedFrom":sQuery(id+"F0.wireOp",EDGE,"E3.4.1.0")}),1.0]])]});
            var Q47;
            Q47=makeQuery(id+"F0.imprint","IMPRINT",FACE,{"disambiguationData":[TD([[makeQuery(id+"F0.imprint","IMPRINT",EDGE,{"derivedFrom":sQuery(id+"F0.wireOp",EDGE,"E3.5.0.0")}),1.0]])]});
            var Q48;
            Q48=makeQuery(id+"F0.imprint","IMPRINT",FACE,{"disambiguationData":[TD([[makeQuery(id+"F0.imprint","IMPRINT",EDGE,{"derivedFrom":sQuery(id+"F0.wireOp",EDGE,"E3.8.2.0")}),1.0]])]});
            var Q49;
            Q49=makeQuery(id+"F0.imprint","IMPRINT",FACE,{"disambiguationData":[TD([[makeQuery(id+"F0.imprint","IMPRINT",EDGE,{"derivedFrom":sQuery(id+"F0.wireOp",EDGE,"E3.3.6.0")}),1.0]])]});
            var Q50;
            Q50=makeQuery(id+"F0.imprint","IMPRINT",FACE,{"disambiguationData":[TD([[makeQuery(id+"F0.imprint","IMPRINT",EDGE,{"derivedFrom":sQuery(id+"F0.wireOp",EDGE,"E4.0.8.8")}),1.0]])]});
            var Q51;
            Q51=makeQuery(id+"F0.imprint","IMPRINT",FACE,{"disambiguationData":[TD([[makeQuery(id+"F0.imprint","IMPRINT",EDGE,{"derivedFrom":sQuery(id+"F0.wireOp",EDGE,"E5.5.5.0")}),1.0]])]});
            var Q52;
            Q52=makeQuery(id+"F0.imprint","IMPRINT",FACE,{"disambiguationData":[TD([[makeQuery(id+"F0.imprint","IMPRINT",EDGE,{"derivedFrom":sQuery(id+"F0.wireOp",EDGE,"E5.2.0.0")}),1.0]])]});
            var Q53;
            Q53=makeQuery(id+"F0.imprint","IMPRINT",FACE,{"disambiguationData":[TD([[makeQuery(id+"F0.imprint","IMPRINT",EDGE,{"derivedFrom":sQuery(id+"F0.wireOp",EDGE,"E3.7.4.0")}),1.0]])]});
            var Q54;
            Q54=makeQuery(id+"F0.imprint","IMPRINT",FACE,{"disambiguationData":[TD([[makeQuery(id+"F0.imprint","IMPRINT",EDGE,{"derivedFrom":sQuery(id+"F0.wireOp",EDGE,"E5.8.1.0")}),1.0]])]});
            var Q55;
            Q55=makeQuery(id+"F0.imprint","IMPRINT",FACE,{"disambiguationData":[TD([[makeQuery(id+"F0.imprint","IMPRINT",EDGE,{"derivedFrom":sQuery(id+"F0.wireOp",EDGE,"E3.3.4.0")}),1.0]])]});
            var Q56;
            Q56=makeQuery(id+"F0.imprint","IMPRINT",FACE,{"disambiguationData":[TD([[makeQuery(id+"F0.imprint","IMPRINT",EDGE,{"derivedFrom":sQuery(id+"F0.wireOp",EDGE,"E3.0.6.0")}),1.0]])]});
            var Q57;
            Q57=makeQuery(id+"F0.imprint","IMPRINT",FACE,{"disambiguationData":[TD([[makeQuery(id+"F0.imprint","IMPRINT",EDGE,{"derivedFrom":sQuery(id+"F0.wireOp",EDGE,"E3.6.7.0")}),1.0]])]});
            var Q58;
            Q58=makeQuery(id+"F0.imprint","IMPRINT",FACE,{"disambiguationData":[TD([[makeQuery(id+"F0.imprint","IMPRINT",EDGE,{"derivedFrom":sQuery(id+"F0.wireOp",EDGE,"E3.0.3.0")}),1.0]])]});
            var Q59;
            Q59=makeQuery(id+"F0.imprint","IMPRINT",FACE,{"disambiguationData":[TD([[makeQuery(id+"F0.imprint","IMPRINT",EDGE,{"derivedFrom":sQuery(id+"F0.wireOp",EDGE,"E5.8.7.0")}),1.0]])]});
            var Q60;
            Q60=makeQuery(id+"F0.imprint","IMPRINT",FACE,{"disambiguationData":[TD([[makeQuery(id+"F0.imprint","IMPRINT",EDGE,{"derivedFrom":sQuery(id+"F0.wireOp",EDGE,"E5.7.3.0")}),1.0]])]});
            var Q61;
            Q61=makeQuery(id+"F0.imprint","IMPRINT",FACE,{"disambiguationData":[TD([[makeQuery(id+"F0.imprint","IMPRINT",EDGE,{"derivedFrom":sQuery(id+"F0.wireOp",EDGE,"E5.5.6.0")}),1.0]])]});
            var Q62;
            Q62=makeQuery(id+"F0.imprint","IMPRINT",FACE,{"disambiguationData":[TD([[makeQuery(id+"F0.imprint","IMPRINT",EDGE,{"derivedFrom":sQuery(id+"F0.wireOp",EDGE,"E4.0.0.8")}),1.0]])]});
            var Q63;
            Q63=makeQuery(id+"F0.imprint","IMPRINT",FACE,{"disambiguationData":[TD([[makeQuery(id+"F0.imprint","IMPRINT",EDGE,{"derivedFrom":sQuery(id+"F0.wireOp",EDGE,"E3.2.5.0")}),1.0]])]});
            var Q64;
            Q64=makeQuery(id+"F0.imprint","IMPRINT",FACE,{"disambiguationData":[TD([[makeQuery(id+"F0.imprint","IMPRINT",EDGE,{"derivedFrom":sQuery(id+"F0.wireOp",EDGE,"E3.7.5.0")}),1.0]])]});
            var Q65;
            Q65=makeQuery(id+"F0.imprint","IMPRINT",FACE,{"disambiguationData":[TD([[makeQuery(id+"F0.imprint","IMPRINT",EDGE,{"derivedFrom":sQuery(id+"F0.wireOp",EDGE,"E5.6.4.0")}),1.0]])]});
            var Q66;
            Q66=makeQuery(id+"F0.imprint","IMPRINT",FACE,{"disambiguationData":[TD([[makeQuery(id+"F0.imprint","IMPRINT",EDGE,{"derivedFrom":sQuery(id+"F0.wireOp",EDGE,"E3.7.7.0")}),1.0]])]});
            var Q67;
            Q67=makeQuery(id+"F0.imprint","IMPRINT",FACE,{"disambiguationData":[TD([[makeQuery(id+"F0.imprint","IMPRINT",EDGE,{"derivedFrom":sQuery(id+"F0.wireOp",EDGE,"E5.3.8.0")}),1.0]])]});
            var Q68;
            Q68=makeQuery(id+"F0.imprint","IMPRINT",FACE,{"disambiguationData":[TD([[makeQuery(id+"F0.imprint","IMPRINT",EDGE,{"derivedFrom":sQuery(id+"F0.wireOp",EDGE,"E3.8.1.0")}),1.0]])]});
            var Q69;
            Q69=makeQuery(id+"F0.imprint","IMPRINT",FACE,{"disambiguationData":[TD([[makeQuery(id+"F0.imprint","IMPRINT",EDGE,{"derivedFrom":sQuery(id+"F0.wireOp",EDGE,"E3.5.5.0")}),1.0]])]});
            var Q70;
            Q70=makeQuery(id+"F0.imprint","IMPRINT",FACE,{"disambiguationData":[TD([[makeQuery(id+"F0.imprint","IMPRINT",EDGE,{"derivedFrom":sQuery(id+"F0.wireOp",EDGE,"E5.4.2.0")}),1.0]])]});
            var Q71;
            Q71=makeQuery(id+"F0.imprint","IMPRINT",FACE,{"disambiguationData":[TD([[makeQuery(id+"F0.imprint","IMPRINT",EDGE,{"derivedFrom":sQuery(id+"F0.wireOp",EDGE,"E5.1.5.0")}),1.0]])]});
            var Q72;
            Q72=makeQuery(id+"F0.imprint","IMPRINT",FACE,{"disambiguationData":[TD([[makeQuery(id+"F0.imprint","IMPRINT",EDGE,{"derivedFrom":sQuery(id+"F0.wireOp",EDGE,"E3.0.5.0")}),1.0]])]});
            var Q73;
            Q73=makeQuery(id+"F0.imprint","IMPRINT",FACE,{"disambiguationData":[TD([[makeQuery(id+"F0.imprint","IMPRINT",EDGE,{"derivedFrom":sQuery(id+"F0.wireOp",EDGE,"E3.2.1.0")}),1.0]])]});
            var Q74;
            Q74=makeQuery(id+"F0.imprint","IMPRINT",FACE,{"disambiguationData":[TD([[makeQuery(id+"F0.imprint","IMPRINT",EDGE,{"derivedFrom":sQuery(id+"F0.wireOp",EDGE,"E3.2.0.0")}),1.0]])]});
            var Q75;
            Q75=makeQuery(id+"F0.imprint","IMPRINT",FACE,{"disambiguationData":[TD([[makeQuery(id+"F0.imprint","IMPRINT",EDGE,{"derivedFrom":sQuery(id+"F0.wireOp",EDGE,"E3.6.4.0")}),1.0]])]});
            var Q76;
            Q76=makeQuery(id+"F0.imprint","IMPRINT",FACE,{"disambiguationData":[TD([[makeQuery(id+"F0.imprint","IMPRINT",EDGE,{"derivedFrom":sQuery(id+"F0.wireOp",EDGE,"E3.5.2.0")}),1.0]])]});
            var Q77;
            Q77=makeQuery(id+"F0.imprint","IMPRINT",FACE,{"disambiguationData":[TD([[makeQuery(id+"F0.imprint","IMPRINT",EDGE,{"derivedFrom":sQuery(id+"F0.wireOp",EDGE,"E4.0.6.8")}),1.0]])]});
            var Q78;
            Q78=makeQuery(id+"F0.imprint","IMPRINT",FACE,{"disambiguationData":[TD([[makeQuery(id+"F0.imprint","IMPRINT",EDGE,{"derivedFrom":sQuery(id+"F0.wireOp",EDGE,"E4.0.2.8")}),1.0]])]});
            var Q79;
            Q79=makeQuery(id+"F0.imprint","IMPRINT",FACE,{"disambiguationData":[TD([[makeQuery(id+"F0.imprint","IMPRINT",EDGE,{"derivedFrom":sQuery(id+"F0.wireOp",EDGE,"E4.0.3.8")}),1.0]])]});
            var Q80;
            Q80=makeQuery(id+"F0.imprint","IMPRINT",FACE,{"disambiguationData":[TD([[makeQuery(id+"F0.imprint","IMPRINT",EDGE,{"derivedFrom":sQuery(id+"F0.wireOp",EDGE,"E5.4.7.0")}),1.0]])]});
            var Q81;
            Q81=makeQuery(id+"F0.imprint","IMPRINT",FACE,{"disambiguationData":[TD([[makeQuery(id+"F0.imprint","IMPRINT",EDGE,{"derivedFrom":sQuery(id+"F0.wireOp",EDGE,"E3.8.7.0")}),1.0]])]});
            var Q82;
            Q82=makeQuery(id+"F0.imprint","IMPRINT",FACE,{"disambiguationData":[TD([[makeQuery(id+"F0.imprint","IMPRINT",EDGE,{"derivedFrom":sQuery(id+"F0.wireOp",EDGE,"E4.0.4.8")}),1.0]])]});
            var Q83;
            Q83=makeQuery(id+"F0.imprint","IMPRINT",FACE,{"disambiguationData":[TD([[makeQuery(id+"F0.imprint","IMPRINT",EDGE,{"derivedFrom":sQuery(id+"F0.wireOp",EDGE,"E3.5.1.0")}),1.0]])]});
            var Q84;
            Q84=makeQuery(id+"F0.imprint","IMPRINT",FACE,{"disambiguationData":[TD([[makeQuery(id+"F0.imprint","IMPRINT",EDGE,{"derivedFrom":sQuery(id+"F0.wireOp",EDGE,"E3.0.4.0")}),1.0]])]});
            var Q85;
            Q85=makeQuery(id+"F0.imprint","IMPRINT",FACE,{"disambiguationData":[TD([[makeQuery(id+"F0.imprint","IMPRINT",EDGE,{"derivedFrom":sQuery(id+"F0.wireOp",EDGE,"E5.3.7.0")}),1.0]])]});
            var Q86;
            Q86=makeQuery(id+"F0.imprint","IMPRINT",FACE,{"disambiguationData":[TD([[makeQuery(id+"F0.imprint","IMPRINT",EDGE,{"derivedFrom":sQuery(id+"F0.wireOp",EDGE,"E5.7.7.0")}),1.0]])]});
            var Q87;
            Q87=makeQuery(id+"F0.imprint","IMPRINT",FACE,{"disambiguationData":[TD([[makeQuery(id+"F0.imprint","IMPRINT",EDGE,{"derivedFrom":sQuery(id+"F0.wireOp",EDGE,"E5.8.2.0")}),1.0]])]});
            var Q88;
            Q88=makeQuery(id+"F0.imprint","IMPRINT",FACE,{"disambiguationData":[TD([[makeQuery(id+"F0.imprint","IMPRINT",EDGE,{"derivedFrom":sQuery(id+"F0.wireOp",EDGE,"E1")}),1.0]])]});
            var Q89;
            Q89=makeQuery(id+"F0.imprint","IMPRINT",FACE,{"disambiguationData":[TD([[makeQuery(id+"F0.imprint","IMPRINT",EDGE,{"derivedFrom":sQuery(id+"F0.wireOp",EDGE,"E3.6.2.0")}),1.0]])]});
            var Q90;
            Q90=makeQuery(id+"F0.imprint","IMPRINT",FACE,{"disambiguationData":[TD([[makeQuery(id+"F0.imprint","IMPRINT",EDGE,{"derivedFrom":sQuery(id+"F0.wireOp",EDGE,"E3.2.4.0")}),1.0]])]});
            var Q91;
            Q91=makeQuery(id+"F0.imprint","IMPRINT",FACE,{"disambiguationData":[TD([[makeQuery(id+"F0.imprint","IMPRINT",EDGE,{"derivedFrom":sQuery(id+"F0.wireOp",EDGE,"E3.8.0.0")}),1.0]])]});
            var Q92;
            Q92=makeQuery(id+"F0.imprint","IMPRINT",FACE,{"disambiguationData":[TD([[makeQuery(id+"F0.imprint","IMPRINT",EDGE,{"derivedFrom":sQuery(id+"F0.wireOp",EDGE,"E3.0.7.0")}),1.0]])]});
            var Q93;
            Q93=makeQuery(id+"F0.imprint","IMPRINT",FACE,{"disambiguationData":[TD([[makeQuery(id+"F0.imprint","IMPRINT",EDGE,{"derivedFrom":sQuery(id+"F0.wireOp",EDGE,"E5.3.4.0")}),1.0]])]});
            var Q94;
            Q94=makeQuery(id+"F0.imprint","IMPRINT",FACE,{"disambiguationData":[TD([[makeQuery(id+"F0.imprint","IMPRINT",EDGE,{"derivedFrom":sQuery(id+"F0.wireOp",EDGE,"E3.5.4.0")}),1.0]])]});
            var Q95;
            Q95=makeQuery(id+"F0.imprint","IMPRINT",FACE,{"disambiguationData":[TD([[makeQuery(id+"F0.imprint","IMPRINT",EDGE,{"derivedFrom":sQuery(id+"F0.wireOp",EDGE,"E5.2.8.0")}),1.0]])]});
            var Q96;
            Q96=makeQuery(id+"F0.imprint","IMPRINT",FACE,{"disambiguationData":[TD([[makeQuery(id+"F0.imprint","IMPRINT",EDGE,{"derivedFrom":sQuery(id+"F0.wireOp",EDGE,"E5.6.6.0")}),1.0]])]});
            var Q97;
            Q97=makeQuery(id+"F0.imprint","IMPRINT",FACE,{"disambiguationData":[TD([[makeQuery(id+"F0.imprint","IMPRINT",EDGE,{"derivedFrom":sQuery(id+"F0.wireOp",EDGE,"E5.4.8.0")}),1.0]])]});
            var Q98;
            Q98=makeQuery(id+"F0.imprint","IMPRINT",FACE,{"disambiguationData":[TD([[makeQuery(id+"F0.imprint","IMPRINT",EDGE,{"derivedFrom":sQuery(id+"F0.wireOp",EDGE,"E5.7.4.0")}),1.0]])]});
            var Q99;
            Q99=makeQuery(id+"F0.imprint","IMPRINT",FACE,{"disambiguationData":[TD([[makeQuery(id+"F0.imprint","IMPRINT",EDGE,{"derivedFrom":sQuery(id+"F0.wireOp",EDGE,"E3.0.2.0")}),1.0]])]});
            var Q100;
            Q100=makeQuery(id+"F0.imprint","IMPRINT",FACE,{"disambiguationData":[TD([[makeQuery(id+"F0.imprint","IMPRINT",EDGE,{"derivedFrom":sQuery(id+"F0.wireOp",EDGE,"E3.5.6.0")}),1.0]])]});
            var Q101;
            Q101=makeQuery(id+"F0.imprint","IMPRINT",FACE,{"disambiguationData":[TD([[makeQuery(id+"F0.imprint","IMPRINT",EDGE,{"derivedFrom":sQuery(id+"F0.wireOp",EDGE,"E5.4.6.0")}),1.0]])]});
            var Q102;
            Q102=makeQuery(id+"F0.imprint","IMPRINT",FACE,{"disambiguationData":[TD([[makeQuery(id+"F0.imprint","IMPRINT",EDGE,{"derivedFrom":sQuery(id+"F0.wireOp",EDGE,"E3.1.6.0")}),1.0]])]});
            var Q103;
            Q103=makeQuery(id+"F0.imprint","IMPRINT",FACE,{"disambiguationData":[TD([[makeQuery(id+"F0.imprint","IMPRINT",EDGE,{"derivedFrom":sQuery(id+"F0.wireOp",EDGE,"E3.6.3.0")}),1.0]])]});
            var Q104;
            Q104=makeQuery(id+"F0.imprint","IMPRINT",FACE,{"disambiguationData":[TD([[makeQuery(id+"F0.imprint","IMPRINT",EDGE,{"derivedFrom":sQuery(id+"F0.wireOp",EDGE,"E3.3.3.0")}),1.0]])]});
            var Q105;
            Q105=makeQuery(id+"F0.imprint","IMPRINT",FACE,{"disambiguationData":[TD([[makeQuery(id+"F0.imprint","IMPRINT",EDGE,{"derivedFrom":sQuery(id+"F0.wireOp",EDGE,"E3.1.3.0")}),1.0]])]});
            var Q106;
            Q106=makeQuery(id+"F0.imprint","IMPRINT",FACE,{"disambiguationData":[TD([[makeQuery(id+"F0.imprint","IMPRINT",EDGE,{"derivedFrom":sQuery(id+"F0.wireOp",EDGE,"E3.1.7.0")}),1.0]])]});
            var Q107;
            Q107=makeQuery(id+"F0.imprint","IMPRINT",FACE,{"disambiguationData":[TD([[makeQuery(id+"F0.imprint","IMPRINT",EDGE,{"derivedFrom":sQuery(id+"F0.wireOp",EDGE,"E3.3.7.0")}),1.0]])]});
            var Q108;
            Q108=makeQuery(id+"F0.imprint","IMPRINT",FACE,{"disambiguationData":[TD([[makeQuery(id+"F0.imprint","IMPRINT",EDGE,{"derivedFrom":sQuery(id+"F0.wireOp",EDGE,"E5.8.3.0")}),1.0]])]});
            var Q109;
            Q109=makeQuery(id+"F0.imprint","IMPRINT",FACE,{"disambiguationData":[TD([[makeQuery(id+"F0.imprint","IMPRINT",EDGE,{"derivedFrom":sQuery(id+"F0.wireOp",EDGE,"E5.4.0.0")}),1.0]])]});
            var Q110;
            Q110=makeQuery(id+"F0.imprint","IMPRINT",FACE,{"disambiguationData":[TD([[makeQuery(id+"F0.imprint","IMPRINT",EDGE,{"derivedFrom":sQuery(id+"F0.wireOp",EDGE,"E5.0.1.0")}),1.0]])]});
            var Q111;
            Q111=makeQuery(id+"F0.imprint","IMPRINT",FACE,{"disambiguationData":[TD([[makeQuery(id+"F0.imprint","IMPRINT",EDGE,{"derivedFrom":sQuery(id+"F0.wireOp",EDGE,"E5.1.0.0")}),1.0]])]});
            var Q112;
            Q112=makeQuery(id+"F0.imprint","IMPRINT",FACE,{"disambiguationData":[TD([[makeQuery(id+"F0.imprint","IMPRINT",EDGE,{"derivedFrom":sQuery(id+"F0.wireOp",EDGE,"E3.6.5.0")}),1.0]])]});
            var Q113;
            Q113=makeQuery(id+"F0.imprint","IMPRINT",FACE,{"disambiguationData":[TD([[makeQuery(id+"F0.imprint","IMPRINT",EDGE,{"derivedFrom":sQuery(id+"F0.wireOp",EDGE,"E5.8.8.0")}),1.0]])]});
            var Q114;
            Q114=makeQuery(id+"F0.imprint","IMPRINT",FACE,{"disambiguationData":[TD([[makeQuery(id+"F0.imprint","IMPRINT",EDGE,{"derivedFrom":sQuery(id+"F0.wireOp",EDGE,"E3.7.3.0")}),1.0]])]});
            var Q115;
            Q115=makeQuery(id+"F0.imprint","IMPRINT",FACE,{"disambiguationData":[TD([[makeQuery(id+"F0.imprint","IMPRINT",EDGE,{"derivedFrom":sQuery(id+"F0.wireOp",EDGE,"E3.7.6.0")}),1.0]])]});
            var Q116;
            Q116=makeQuery(id+"F0.imprint","IMPRINT",FACE,{"disambiguationData":[TD([[makeQuery(id+"F0.imprint","IMPRINT",EDGE,{"derivedFrom":sQuery(id+"F0.wireOp",EDGE,"E3.4.3.0")}),1.0]])]});
            var Q117;
            Q117=makeQuery(id+"F0.imprint","IMPRINT",FACE,{"disambiguationData":[TD([[makeQuery(id+"F0.imprint","IMPRINT",EDGE,{"derivedFrom":sQuery(id+"F0.wireOp",EDGE,"E3.8.3.0")}),1.0]])]});
            var Q118;
            Q118=makeQuery(id+"F0.imprint","IMPRINT",FACE,{"disambiguationData":[TD([[makeQuery(id+"F0.imprint","IMPRINT",EDGE,{"derivedFrom":sQuery(id+"F0.wireOp",EDGE,"E3.6.1.0")}),1.0]])]});
            var Q119;
            Q119=makeQuery(id+"F0.imprint","IMPRINT",FACE,{"disambiguationData":[TD([[makeQuery(id+"F0.imprint","IMPRINT",EDGE,{"derivedFrom":sQuery(id+"F0.wireOp",EDGE,"E3.0.1.0")}),1.0]])]});
            var Q120;
            Q120=makeQuery(id+"F0.imprint","IMPRINT",FACE,{"disambiguationData":[TD([[makeQuery(id+"F0.imprint","IMPRINT",EDGE,{"derivedFrom":sQuery(id+"F0.wireOp",EDGE,"E5.7.0.0")}),1.0]])]});
            var Q121;
            Q121=makeQuery(id+"F0.imprint","IMPRINT",FACE,{"disambiguationData":[TD([[makeQuery(id+"F0.imprint","IMPRINT",EDGE,{"derivedFrom":sQuery(id+"F0.wireOp",EDGE,"E3.2.2.0")}),1.0]])]});
            var Q122;
            Q122=makeQuery(id+"F0.imprint","IMPRINT",FACE,{"disambiguationData":[TD([[makeQuery(id+"F0.imprint","IMPRINT",EDGE,{"derivedFrom":sQuery(id+"F0.wireOp",EDGE,"E5.1.1.0")}),1.0]])]});
            var Q123;
            Q123=makeQuery(id+"F0.imprint","IMPRINT",FACE,{"disambiguationData":[TD([[makeQuery(id+"F0.imprint","IMPRINT",EDGE,{"derivedFrom":sQuery(id+"F0.wireOp",EDGE,"E5.6.8.0")}),1.0]])]});
            var Q124;
            Q124=makeQuery(id+"F0.imprint","IMPRINT",FACE,{"disambiguationData":[TD([[makeQuery(id+"F0.imprint","IMPRINT",EDGE,{"derivedFrom":sQuery(id+"F0.wireOp",EDGE,"E5.0.2.0")}),1.0]])]});
            var Q125;
            Q125=makeQuery(id+"F0.imprint","IMPRINT",FACE,{"disambiguationData":[TD([[makeQuery(id+"F0.imprint","IMPRINT",EDGE,{"derivedFrom":sQuery(id+"F0.wireOp",EDGE,"E3.2.7.0")}),1.0]])]});
            var Q126;
            Q126=makeQuery(id+"F0.imprint","IMPRINT",FACE,{"disambiguationData":[TD([[makeQuery(id+"F0.imprint","IMPRINT",EDGE,{"derivedFrom":sQuery(id+"F0.wireOp",EDGE,"E5.4.1.0")}),1.0]])]});
            var Q127;
            Q127=makeQuery(id+"F0.imprint","IMPRINT",FACE,{"disambiguationData":[TD([[makeQuery(id+"F0.imprint","IMPRINT",EDGE,{"derivedFrom":sQuery(id+"F0.wireOp",EDGE,"E5.5.3.0")}),1.0]])]});
            var Q128;
            Q128=makeQuery(id+"F0.imprint","IMPRINT",FACE,{"disambiguationData":[TD([[makeQuery(id+"F0.imprint","IMPRINT",EDGE,{"derivedFrom":sQuery(id+"F0.wireOp",EDGE,"E5.1.6.0")}),1.0]])]});
            var Q129;
            Q129=makeQuery(id+"F0.imprint","IMPRINT",FACE,{"disambiguationData":[TD([[makeQuery(id+"F0.imprint","IMPRINT",EDGE,{"derivedFrom":sQuery(id+"F0.wireOp",EDGE,"E5.7.1.0")}),1.0]])]});
            var Q130;
            Q130=makeQuery(id+"F0.imprint","IMPRINT",FACE,{"disambiguationData":[TD([[makeQuery(id+"F0.imprint","IMPRINT",EDGE,{"derivedFrom":sQuery(id+"F0.wireOp",EDGE,"E5.7.6.0")}),1.0]])]});
            var Q131;
            Q131=makeQuery(id+"F0.imprint","IMPRINT",FACE,{"disambiguationData":[TD([[makeQuery(id+"F0.imprint","IMPRINT",EDGE,{"derivedFrom":sQuery(id+"F0.wireOp",EDGE,"E5.1.3.0")}),1.0]])]});
            var Q132;
            Q132=makeQuery(id+"F0.imprint","IMPRINT",FACE,{"disambiguationData":[TD([[makeQuery(id+"F0.imprint","IMPRINT",EDGE,{"derivedFrom":sQuery(id+"F0.wireOp",EDGE,"E5.6.3.0")}),1.0]])]});
            var Q133;
            Q133=makeQuery(id+"F0.imprint","IMPRINT",FACE,{"disambiguationData":[TD([[makeQuery(id+"F0.imprint","IMPRINT",EDGE,{"derivedFrom":sQuery(id+"F0.wireOp",EDGE,"E5.8.5.0")}),1.0]])]});
            var Q134;
            Q134=makeQuery(id+"F0.imprint","IMPRINT",FACE,{"disambiguationData":[TD([[makeQuery(id+"F0.imprint","IMPRINT",EDGE,{"derivedFrom":sQuery(id+"F0.wireOp",EDGE,"E5.5.7.0")}),1.0]])]});
            var Q135;
            Q135=makeQuery(id+"F0.imprint","IMPRINT",FACE,{"disambiguationData":[TD([[makeQuery(id+"F0.imprint","IMPRINT",EDGE,{"derivedFrom":sQuery(id+"F0.wireOp",EDGE,"E5.1.7.0")}),1.0]])]});
            var Q136;
            Q136=makeQuery(id+"F0.imprint","IMPRINT",FACE,{"disambiguationData":[TD([[makeQuery(id+"F0.imprint","IMPRINT",EDGE,{"derivedFrom":sQuery(id+"F0.wireOp",EDGE,"E5.7.5.0")}),1.0]])]});
            var Q137;
            Q137=makeQuery(id+"F0.imprint","IMPRINT",FACE,{"disambiguationData":[TD([[makeQuery(id+"F0.imprint","IMPRINT",EDGE,{"derivedFrom":sQuery(id+"F0.wireOp",EDGE,"E5.8.0.0")}),1.0]])]});
            var Q138;
            Q138=makeQuery(id+"F0.imprint","IMPRINT",FACE,{"disambiguationData":[TD([[makeQuery(id+"F0.imprint","IMPRINT",EDGE,{"derivedFrom":sQuery(id+"F0.wireOp",EDGE,"E5.2.7.0")}),1.0]])]});
            var Q139;
            Q139=makeQuery(id+"F0.imprint","IMPRINT",FACE,{"disambiguationData":[TD([[makeQuery(id+"F0.imprint","IMPRINT",EDGE,{"derivedFrom":sQuery(id+"F0.wireOp",EDGE,"E5.6.7.0")}),1.0]])]});
            var Q140;
            Q140=makeQuery(id+"F0.imprint","IMPRINT",FACE,{"disambiguationData":[TD([[makeQuery(id+"F0.imprint","IMPRINT",EDGE,{"derivedFrom":sQuery(id+"F0.wireOp",EDGE,"E5.2.1.0")}),1.0]])]});
            var Q141;
            Q141=makeQuery(id+"F0.imprint","IMPRINT",FACE,{"disambiguationData":[TD([[makeQuery(id+"F0.imprint","IMPRINT",EDGE,{"derivedFrom":sQuery(id+"F0.wireOp",EDGE,"E5.4.4.0")}),1.0]])]});
            var Q142;
            Q142=makeQuery(id+"F0.imprint","IMPRINT",FACE,{"disambiguationData":[TD([[makeQuery(id+"F0.imprint","IMPRINT",EDGE,{"derivedFrom":sQuery(id+"F0.wireOp",EDGE,"E5.3.5.0")}),1.0]])]});
            var Q143;
            Q143=makeQuery(id+"F0.imprint","IMPRINT",FACE,{"disambiguationData":[TD([[makeQuery(id+"F0.imprint","IMPRINT",EDGE,{"derivedFrom":sQuery(id+"F0.wireOp",EDGE,"E5.3.1.0")}),1.0]])]});
            var Q144;
            Q144=makeQuery(id+"F0.imprint","IMPRINT",FACE,{"disambiguationData":[TD([[makeQuery(id+"F0.imprint","IMPRINT",EDGE,{"derivedFrom":sQuery(id+"F0.wireOp",EDGE,"E5.0.8.0")}),1.0]])]});
            var Q145;
            Q145=makeQuery(id+"F0.imprint","IMPRINT",FACE,{"disambiguationData":[TD([[makeQuery(id+"F0.imprint","IMPRINT",EDGE,{"derivedFrom":sQuery(id+"F0.wireOp",EDGE,"E5.2.6.0")}),1.0]])]});
            var Q146;
            Q146=makeQuery(id+"F0.imprint","IMPRINT",FACE,{"disambiguationData":[TD([[makeQuery(id+"F0.imprint","IMPRINT",EDGE,{"derivedFrom":sQuery(id+"F0.wireOp",EDGE,"E5.1.8.0")}),1.0]])]});
            var Q147;
            Q147=makeQuery(id+"F0.imprint","IMPRINT",FACE,{"disambiguationData":[TD([[makeQuery(id+"F0.imprint","IMPRINT",EDGE,{"derivedFrom":sQuery(id+"F0.wireOp",EDGE,"E5.5.8.0")}),1.0]])]});
            var Q148;
            Q148=makeQuery(id+"F0.imprint","IMPRINT",FACE,{"disambiguationData":[TD([[makeQuery(id+"F0.imprint","IMPRINT",EDGE,{"derivedFrom":sQuery(id+"F0.wireOp",EDGE,"E5.3.2.0")}),1.0]])]});
            var Q149;
            Q149=makeQuery(id+"F0.imprint","IMPRINT",FACE,{"disambiguationData":[TD([[makeQuery(id+"F0.imprint","IMPRINT",EDGE,{"derivedFrom":sQuery(id+"F0.wireOp",EDGE,"E5.5.4.0")}),1.0]])]});
            var Q150;
            Q150=makeQuery(id+"F0.imprint","IMPRINT",FACE,{"disambiguationData":[TD([[makeQuery(id+"F0.imprint","IMPRINT",EDGE,{"derivedFrom":sQuery(id+"F0.wireOp",EDGE,"E5.2.5.0")}),1.0]])]});
            var Q151;
            Q151=makeQuery(id+"F0.imprint","IMPRINT",FACE,{"disambiguationData":[TD([[makeQuery(id+"F0.imprint","IMPRINT",EDGE,{"derivedFrom":sQuery(id+"F0.wireOp",EDGE,"E5.2.2.0")}),1.0]])]});
            var Q152;
            Q152=makeQuery(id+"F0.imprint","IMPRINT",FACE,{"disambiguationData":[TD([[makeQuery(id+"F0.imprint","IMPRINT",EDGE,{"derivedFrom":sQuery(id+"F0.wireOp",EDGE,"E5.4.5.0")}),1.0]])]});
            var Q153;
            Q153=makeQuery(id+"F0.imprint","IMPRINT",FACE,{"disambiguationData":[TD([[makeQuery(id+"F0.imprint","IMPRINT",EDGE,{"derivedFrom":sQuery(id+"F0.wireOp",EDGE,"E5.3.0.0")}),1.0]])]});
            var Q154;
            Q154=makeQuery(id+"F0.imprint","IMPRINT",FACE,{"disambiguationData":[TD([[makeQuery(id+"F0.imprint","IMPRINT",EDGE,{"derivedFrom":sQuery(id+"F0.wireOp",EDGE,"E5.0.4.0")}),1.0]])]});
            var Q155;
            Q155=makeQuery(id+"F0.imprint","IMPRINT",FACE,{"disambiguationData":[TD([[makeQuery(id+"F0.imprint","IMPRINT",EDGE,{"derivedFrom":sQuery(id+"F0.wireOp",EDGE,"E5.1.4.0")}),1.0]])]});
            var Q156;
            Q156=makeQuery(id+"F0.imprint","IMPRINT",FACE,{"disambiguationData":[TD([[makeQuery(id+"F0.imprint","IMPRINT",EDGE,{"derivedFrom":sQuery(id+"F0.wireOp",EDGE,"E5.7.2.0")}),1.0]])]});
            var Q157;
            Q157=makeQuery(id+"F0.imprint","IMPRINT",FACE,{"disambiguationData":[TD([[makeQuery(id+"F0.imprint","IMPRINT",EDGE,{"derivedFrom":sQuery(id+"F0.wireOp",EDGE,"E5.6.2.0")}),1.0]])]});
            var Q158;
            Q158=makeQuery(id+"F0.imprint","IMPRINT",FACE,{"disambiguationData":[TD([[makeQuery(id+"F0.imprint","IMPRINT",EDGE,{"derivedFrom":sQuery(id+"F0.wireOp",EDGE,"E5.1.2.0")}),1.0]])]});
            var Q159;
            Q159=makeQuery(id+"F0.imprint","IMPRINT",FACE,{"disambiguationData":[TD([[makeQuery(id+"F0.imprint","IMPRINT",EDGE,{"derivedFrom":sQuery(id+"F0.wireOp",EDGE,"E5.0.3.0")}),1.0]])]});
            var Q160;
            Q160=makeQuery(id+"F0.imprint","IMPRINT",FACE,{"disambiguationData":[TD([[makeQuery(id+"F0.imprint","IMPRINT",EDGE,{"derivedFrom":sQuery(id+"F0.wireOp",EDGE,"E5.3.6.0")}),1.0]])]});
            var Q161;
            Q161=makeQuery(id+"F0.imprint","IMPRINT",FACE,{"disambiguationData":[TD([[makeQuery(id+"F0.imprint","IMPRINT",EDGE,{"derivedFrom":sQuery(id+"F0.wireOp",EDGE,"E5.8.4.0")}),1.0]])]});
            var Q162;
            Q162=makeQuery(id+"F0.imprint","IMPRINT",FACE,{"disambiguationData":[TD([[makeQuery(id+"F0.imprint","IMPRINT",EDGE,{"derivedFrom":sQuery(id+"F0.wireOp",EDGE,"E2")}),1.0]])]});
            extrude(context, id + "F1", {"entities" : qUnion([Q0, Q1, Q2, Q3, Q4, Q5, Q6, Q7, Q8, Q9, Q10, Q11, Q12, Q13, Q14, Q15, Q16, Q17, Q18, Q19, Q20, Q21, Q22, Q23, Q24, Q25, Q26, Q27, Q28, Q29, Q30, Q31, Q32, Q33, Q34, Q35, Q36, Q37, Q38, Q39, Q40, Q41, Q42, Q43, Q44, Q45, Q46, Q47, Q48, Q49, Q50, Q51, Q52, Q53, Q54, Q55, Q56, Q57, Q58, Q59, Q60, Q61, Q62, Q63, Q64, Q65, Q66, Q67, Q68, Q69, Q70, Q71, Q72, Q73, Q74, Q75, Q76, Q77, Q78, Q79, Q80, Q81, Q82, Q83, Q84, Q85, Q86, Q87, Q88, Q89, Q90, Q91, Q92, Q93, Q94, Q95, Q96, Q97, Q98, Q99, Q100, Q101, Q102, Q103, Q104, Q105, Q106, Q107, Q108, Q109, Q110, Q111, Q112, Q113, Q114, Q115, Q116, Q117, Q118, Q119, Q120, Q121, Q122, Q123, Q124, Q125, Q126, Q127, Q128, Q129, Q130, Q131, Q132, Q133, Q134, Q135, Q136, Q137, Q138, Q139, Q140, Q141, Q142, Q143, Q144, Q145, Q146, Q147, Q148, Q149, Q150, Q151, Q152, Q153, Q154, Q155, Q156, Q157, Q158, Q159, Q160, Q161, Q162]), "oppositeDirection" : true, "depth" : 3.17 * mm, "offsetDistance" : 25.4 * mm});
        }
        {
            var Q0;
            Q0=makeQuery(id+"F0.imprint","IMPRINT",FACE,{"disambiguationData":[TD([[makeQuery(id+"F0.imprint","IMPRINT",EDGE,{"derivedFrom":sQuery(id+"F0.wireOp",EDGE,"E0.bottom")}),1.0]])]});
            extrude(context, id + "F2", {"entities" : qUnion([Q0]), "operationType" : NewBodyOperationType.ADD, "depth" : 6.35 * mm, "offsetDistance" : 25.4 * mm});
        }
        {
            var Q0;
            {var subQ0=sQuery(id+"F0.wireOp",EDGE,"E0.right");var subQ1=sQuery(id+"F0.wireOp",EDGE,"E0.bottom");Q0=makeQuery(id+"F2.boolean.opBoolean","MERGE",EDGE,{"derivedFrom":[makeQuery(id+"F1.opExtrude","SWEPT_EDGE",EDGE,{"disambiguationData":[OSD([subQ1,subQ0])]}),makeQuery(id+"F2.opExtrude","SWEPT_EDGE",EDGE,{"disambiguationData":[OSD([subQ1,subQ0])]})]});}
            var Q1;
            {var subQ0=sQuery(id+"F0.wireOp",EDGE,"E0.left");var subQ1=sQuery(id+"F0.wireOp",EDGE,"E0.bottom");Q1=makeQuery(id+"F2.boolean.opBoolean","MERGE",EDGE,{"derivedFrom":[makeQuery(id+"F1.opExtrude","SWEPT_EDGE",EDGE,{"disambiguationData":[OSD([subQ1,subQ0])]}),makeQuery(id+"F2.opExtrude","SWEPT_EDGE",EDGE,{"disambiguationData":[OSD([subQ1,subQ0])]})]});}
            var Q2;
            {var subQ0=sQuery(id+"F0.wireOp",EDGE,"E0.right");var subQ1=sQuery(id+"F0.wireOp",EDGE,"E0.top");Q2=makeQuery(id+"F2.boolean.opBoolean","MERGE",EDGE,{"derivedFrom":[makeQuery(id+"F1.opExtrude","SWEPT_EDGE",EDGE,{"disambiguationData":[OSD([subQ1,subQ0])]}),makeQuery(id+"F2.opExtrude","SWEPT_EDGE",EDGE,{"disambiguationData":[OSD([subQ1,subQ0])]})]});}
            var Q3;
            {var subQ0=sQuery(id+"F0.wireOp",EDGE,"E0.left");var subQ1=sQuery(id+"F0.wireOp",EDGE,"E0.top");Q3=makeQuery(id+"F2.boolean.opBoolean","MERGE",EDGE,{"derivedFrom":[makeQuery(id+"F1.opExtrude","SWEPT_EDGE",EDGE,{"disambiguationData":[OSD([subQ1,subQ0])]}),makeQuery(id+"F2.opExtrude","SWEPT_EDGE",EDGE,{"disambiguationData":[OSD([subQ1,subQ0])]})]});}
            fillet(context, id + "F3", {"entities" : qUnion([Q0, Q1, Q2, Q3]), "radius" : 6.35 * mm, "tangentPropagation" : true, "allowEdgeOverflow" : false});
        }
    });
